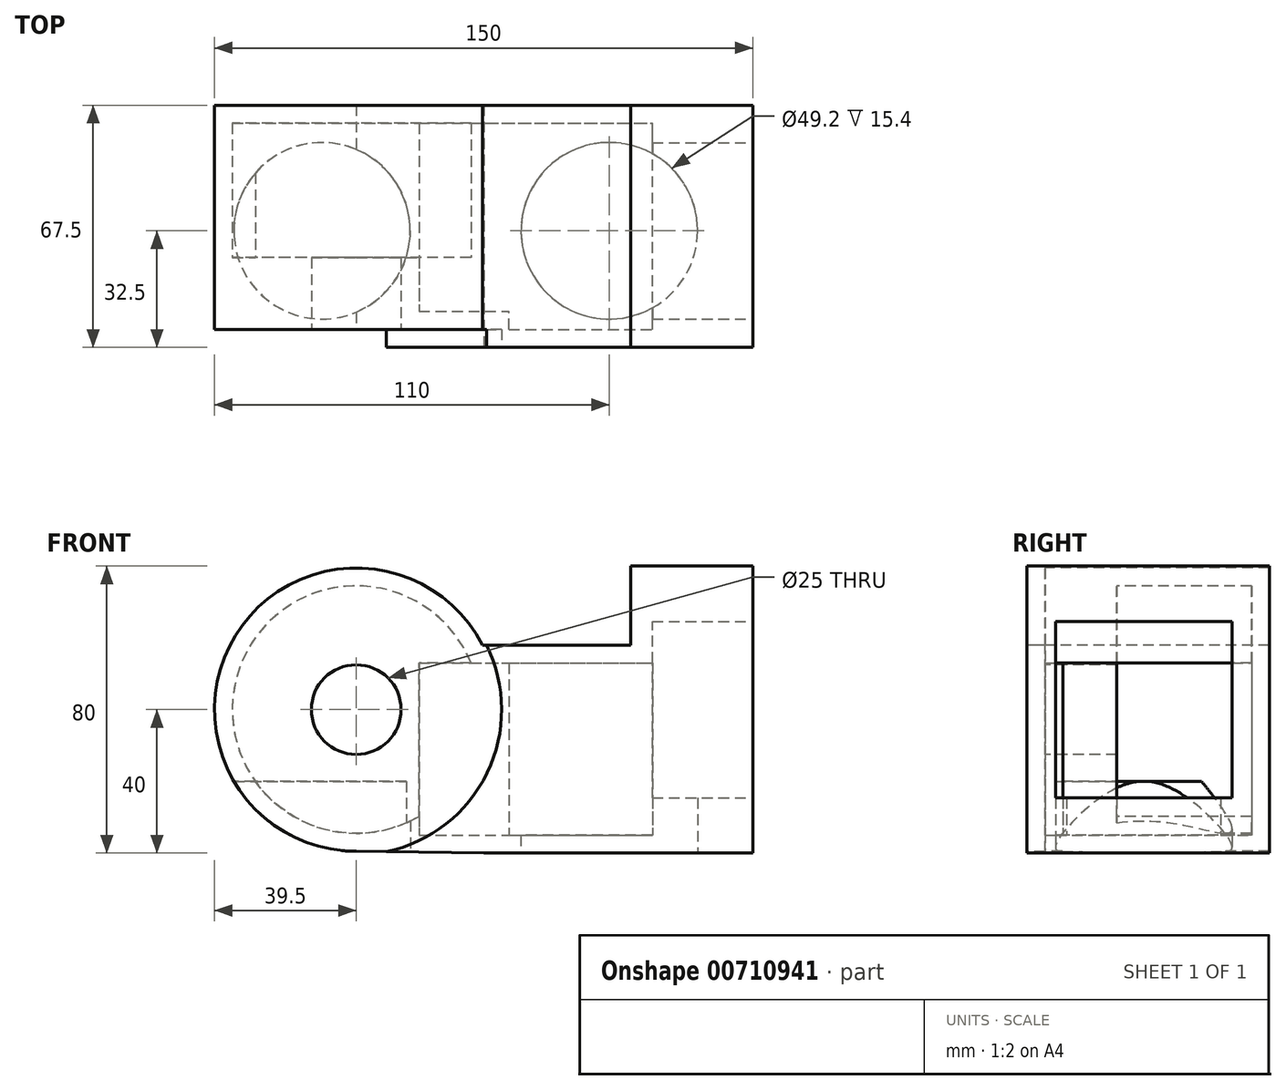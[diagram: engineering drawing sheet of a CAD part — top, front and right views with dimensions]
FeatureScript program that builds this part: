
annotation { "Feature Type Name" : "Feature", "Feature Type Description" : "" }
export const myFeature = defineFeature(function(context is Context, id is Id, definition is map)
    precondition{}
    {
        {
            var Q0;
            Q0=qCreatedBy(makeId("Front.planeOp"),FACE);
            var sketch = newSketch(context, id + "F0", { "sketchPlane" : qUnion([Q0])});
            skCircle(sketch, "E0", {"center": v(-35.5, 40) * mm, "radius": 39.5 * mm});
            skLineSegment(sketch, "E1", {"start": v(0, 0) * mm, "end": v(-35.5, 0.5) * mm});
            skLineSegment(sketch, "E2", {"start": v(0, 0) * mm, "end": v(75, 0) * mm});
            skLineSegment(sketch, "E3", {"start": v(75, 0) * mm, "end": v(75, 80) * mm});
            skLineSegment(sketch, "E4", {"start": v(75, 80) * mm, "end": v(41, 80) * mm});
            skLineSegment(sketch, "E5", {"start": v(41, 80) * mm, "end": v(41, 58) * mm});
            skLineSegment(sketch, "E6", {"start": v(41, 58) * mm, "end": v(-0.34, 58) * mm});
            skSolve(sketch);
        }
        {
            var Q0;
            {var subQ0=sQuery(id+"F0.wireOp",EDGE,"E0");var subQ1=makeQuery(id+"F0.imprint","INTERSECT",VERTEX,{"derivedFrom":[subQ0,sQuery(id+"F0.wireOp",EDGE,"E1")]});Q0=makeQuery(id+"F0.imprint","IMPRINT",FACE,{"disambiguationData":[TD([[makeQuery(id+"F0.imprint","IMPRINT",EDGE,{"disambiguationData":[TD([[subQ1,1.0]])],"derivedFrom":subQ0}),1.0]])]});}
            var Q1;
            {var subQ0=sQuery(id+"F0.wireOp",EDGE,"E1");Q1=makeQuery(id+"F0.imprint","IMPRINT",FACE,{"disambiguationData":[TD([[makeQuery(id+"F0.imprint","IMPRINT",EDGE,{"derivedFrom":subQ0}),-1.0]])]});}
            extrude(context, id + "F1", {"entities" : qUnion([Q0, Q1]), "oppositeDirection" : true, "depth" : 67.5 * mm, "offsetDistance" : 25 * mm});
        }
        {
            var Q0;
            Q0=qCreatedBy(makeId("Right.planeOp"),FACE);
            cPlane(context, id + "F2", {"entities" : qUnion([Q0]), "cplaneType" : CPlaneType.OFFSET, "offset" : 75 * mm, "width" : 150 * mm, "height" : 150 * mm});
        }
        {
            var Q0;
            Q0=qCreatedBy(id+"F2.planeOp",FACE);
            var sketch = newSketch(context, id + "F3", { "sketchPlane" : qUnion([Q0])});
            skPoint(sketch, "E7", {"position": v(32.5, 40) * mm});
            skPoint(sketch, "E8", {"position": v(-7.5, 0) * mm});
            skLineSegment(sketch, "E9.bottom", {"start": v(57.1, 15.4) * mm, "end": v(7.9, 15.4) * mm});
            skLineSegment(sketch, "E9.top", {"start": v(57.1, 64.6) * mm, "end": v(7.9, 64.6) * mm});
            skLineSegment(sketch, "E9.left", {"start": v(57.1, 15.4) * mm, "end": v(57.1, 64.6) * mm});
            skLineSegment(sketch, "E9.right", {"start": v(7.9, 15.4) * mm, "end": v(7.9, 64.6) * mm});
            skLineSegment(sketch, "E10", {"start": v(-7.5, -17.73) * mm, "end": v(71.5, -17.73) * mm});
            skLineSegment(sketch, "E11", {"start": v(71.5, -17.73) * mm, "end": v(71.5, 93.92) * mm});
            skSolve(sketch);
        }
        {
            var Q0;
            Q0=makeQuery(id+"F3.imprint","IMPRINT",FACE,{"disambiguationData":[TD([[makeQuery(id+"F3.imprint","IMPRINT",EDGE,{"derivedFrom":sQuery(id+"F3.wireOp",EDGE,"E9.bottom")}),-1.0]])]});
            extrude(context, id + "F4", {"entities" : qUnion([Q0]), "operationType" : NewBodyOperationType.REMOVE, "oppositeDirection" : true, "depth" : 28 * mm, "offsetDistance" : 25 * mm});
        }
        {
            var Q0;
            Q0=qCreatedBy(makeId("Right.planeOp"),FACE);
            cPlane(context, id + "F5", {"entities" : qUnion([Q0]), "cplaneType" : CPlaneType.OFFSET, "offset" : 47 * mm, "width" : 150 * mm, "height" : 150 * mm});
        }
        {
            var Q0;
            Q0=qCreatedBy(id+"F5.planeOp",FACE);
            var sketch = newSketch(context, id + "F6", { "sketchPlane" : qUnion([Q0])});
            skLineSegment(sketch, "E12.bottom", {"start": v(5, 53) * mm, "end": v(62.5, 53) * mm});
            skLineSegment(sketch, "E12.top", {"start": v(5, 5) * mm, "end": v(62.5, 5) * mm});
            skLineSegment(sketch, "E12.left", {"start": v(5, 53) * mm, "end": v(5, 5) * mm});
            skLineSegment(sketch, "E12.right", {"start": v(62.5, 53) * mm, "end": v(62.5, 5) * mm});
            skSolve(sketch);
        }
        {
            var Q0;
            Q0=makeQuery(id+"F6.imprint","IMPRINT",FACE,{"disambiguationData":[TD([[makeQuery(id+"F6.imprint","IMPRINT",EDGE,{"derivedFrom":sQuery(id+"F6.wireOp",EDGE,"E12.bottom")}),-1.0]])]});
            extrude(context, id + "F7", {"entities" : qUnion([Q0]), "operationType" : NewBodyOperationType.REMOVE, "oppositeDirection" : true, "depth" : 40 * mm, "offsetDistance" : 25 * mm});
        }
        {
            var Q0;
            Q0=makeQuery(id+"F1.opExtrude","CAP_FACE",FACE,{"disambiguationData":[OSD([sQuery(id+"F0.wireOp",EDGE,"E0"),sQuery(id+"F0.wireOp",EDGE,"E1"),sQuery(id+"F0.wireOp",EDGE,"E2"),sQuery(id+"F0.wireOp",EDGE,"E3"),sQuery(id+"F0.wireOp",EDGE,"E4"),sQuery(id+"F0.wireOp",EDGE,"E5"),sQuery(id+"F0.wireOp",EDGE,"E6")])],"isStart":true});
            var sketch = newSketch(context, id + "F8", { "sketchPlane" : qUnion([Q0])});
            skCircle(sketch, "E13", {"center": v(-35.5, 40) * mm, "radius": 40.5 * mm});
            skSolve(sketch);
        }
        {
            var Q0;
            {var subQ5=makeQuery(id+"F1.opExtrude","CAP_EDGE",EDGE,{"disambiguationData":[OSD([sQuery(id+"F0.wireOp",EDGE,"E0")])],"isStart":true});Q0=makeQuery(id+"F8.imprint","IMPRINT",FACE,{"disambiguationData":[TD([[makeQuery(id+"F8.imprint","IMPRINT",EDGE,{"derivedFrom":subQ5}),1.0]])]});}
            extrude(context, id + "F9", {"entities" : qUnion([Q0]), "operationType" : NewBodyOperationType.REMOVE, "oppositeDirection" : true, "depth" : 5 * mm, "offsetDistance" : 25 * mm});
        }
        {
            var Q0;
            Q0=makeQuery(id+"F9.boolean.opBoolean","COPY",FACE,{"derivedFrom":makeQuery(id+"F9.opExtrude","CAP_FACE",FACE,{"disambiguationData":[OSD([sQuery(id+"F0.wireOp",EDGE,"E0"),sQuery(id+"F0.wireOp",EDGE,"E1"),sQuery(id+"F0.wireOp",EDGE,"E6"),sQuery(id+"F8.wireOp",EDGE,"E13")])],"isStart":false})});
            var sketch = newSketch(context, id + "F10", { "sketchPlane" : qUnion([Q0])});
            skCircle(sketch, "E14", {"center": v(-35.5, 40) * mm, "radius": 12.5 * mm});
            skSolve(sketch);
        }
        {
            var Q0;
            Q0=makeQuery(id+"F10.imprint","IMPRINT",FACE,{"disambiguationData":[TD([[makeQuery(id+"F10.imprint","IMPRINT",EDGE,{"derivedFrom":sQuery(id+"F10.wireOp",EDGE,"E14")}),1.0]])]});
            extrude(context, id + "F11", {"entities" : qUnion([Q0]), "operationType" : NewBodyOperationType.REMOVE, "oppositeDirection" : true, "depth" : 20 * mm, "offsetDistance" : 25 * mm});
        }
        {
            var Q0;
            Q0=qCreatedBy(makeId("Front.planeOp"),FACE);
            cPlane(context, id + "F12", {"entities" : qUnion([Q0]), "cplaneType" : CPlaneType.OFFSET, "offset" : 25 * mm, "oppositeDirection" : true, "width" : 150 * mm, "height" : 150 * mm});
        }
        {
            var Q0;
            Q0=qCreatedBy(id+"F12.planeOp",FACE);
            var sketch = newSketch(context, id + "F13", { "sketchPlane" : qUnion([Q0])});
            skCircle(sketch, "E15", {"center": v(-35.5, 40) * mm, "radius": 34.5 * mm});
            skSolve(sketch);
        }
        {
            var Q0;
            Q0=makeQuery(id+"F13.imprint","IMPRINT",FACE,{"disambiguationData":[TD([[makeQuery(id+"F13.imprint","IMPRINT",EDGE,{"derivedFrom":sQuery(id+"F13.wireOp",EDGE,"E15")}),1.0]])]});
            extrude(context, id + "F14", {"entities" : qUnion([Q0]), "operationType" : NewBodyOperationType.REMOVE, "oppositeDirection" : true, "depth" : 37.5 * mm, "offsetDistance" : 25 * mm});
        }
        {
            var Q0;
            Q0=qCreatedBy(makeId("Right.planeOp"),FACE);
            cPlane(context, id + "F15", {"entities" : qUnion([Q0]), "cplaneType" : CPlaneType.OFFSET, "offset" : 7 * mm, "width" : 150 * mm, "height" : 150 * mm});
        }
        {
            var Q0;
            Q0=qCreatedBy(id+"F15.planeOp",FACE);
            var sketch = newSketch(context, id + "F16", { "sketchPlane" : qUnion([Q0])});
            skLineSegment(sketch, "E16.bottom", {"start": v(62.5, 53) * mm, "end": v(10, 53) * mm});
            skLineSegment(sketch, "E16.top", {"start": v(62.5, 5) * mm, "end": v(10, 5) * mm});
            skLineSegment(sketch, "E16.left", {"start": v(62.5, 53) * mm, "end": v(62.5, 5) * mm});
            skLineSegment(sketch, "E16.right", {"start": v(10, 53) * mm, "end": v(10, 5) * mm});
            skSolve(sketch);
        }
        {
            var Q0;
            Q0=makeQuery(id+"F16.imprint","IMPRINT",FACE,{"disambiguationData":[TD([[makeQuery(id+"F16.imprint","IMPRINT",EDGE,{"derivedFrom":sQuery(id+"F16.wireOp",EDGE,"E16.bottom")}),1.0]])]});
            extrude(context, id + "F17", {"entities" : qUnion([Q0]), "operationType" : NewBodyOperationType.REMOVE, "oppositeDirection" : true, "depth" : 25 * mm, "offsetDistance" : 25 * mm});
        }
        {
            var Q0;
            Q0=qCreatedBy(makeId("Top.planeOp"),FACE);
            var sketch = newSketch(context, id + "F18", { "sketchPlane" : qUnion([Q0])});
            skPoint(sketch, "E17", {"position": v(0, -7.5) * mm});
            skCircle(sketch, "E18", {"center": v(35, 32.5) * mm, "radius": 24.6 * mm});
            skCircle(sketch, "E19.1.0.0", {"center": v(-45, 32.5) * mm, "radius": 24.6 * mm});
            skLineSegment(sketch, "E19.direction1", {"start": v(35, 32.5) * mm, "end": v(-45, 32.5) * mm, "construction": true});
            skSolve(sketch);
        }
        {
            var Q0;
            Q0=makeQuery(id+"F18.imprint","IMPRINT",FACE,{"disambiguationData":[TD([[makeQuery(id+"F18.imprint","IMPRINT",EDGE,{"derivedFrom":sQuery(id+"F18.wireOp",EDGE,"E19.1.0.0")}),1.0]])]});
            var Q1;
            Q1=makeQuery(id+"F18.imprint","IMPRINT",FACE,{"disambiguationData":[TD([[makeQuery(id+"F18.imprint","IMPRINT",EDGE,{"derivedFrom":sQuery(id+"F18.wireOp",EDGE,"E18")}),1.0]])]});
            extrude(context, id + "F19", {"entities" : qUnion([Q0, Q1]), "operationType" : NewBodyOperationType.REMOVE, "depth" : 20 * mm, "offsetDistance" : 25 * mm});
        }
    });
